# Revit family: AM 800 HTDE
name_source: partatom
category: Mechanical Equipment
units: mm (PartAtom-declared; Revit-internal decimal feet)

## family parameters
Always vertical = Yes
Cut with Voids When Loaded = No
OmniClass Number = 23.75.00.00
OmniClass Title = Climate Control (HVAC)
Part Type = Normal
Room Calculation Point = No
Round Connector Dimension = Use Diameter
Shared = No
Work Plane-Based = No

## types (1)
- AM 800 HTDE
    BMS IN = (PTS) 2x2x0,6
    BMS Out = (PTS) 2x2x0,6
    BMS Panel = (PTS) 2x2x0,6
    Condensate = 9 mm  [stored 0.0295276 ft]
    Electrical connection = 1 ~ 230 V / N / PE / 50 Hz
    Exhaust Air = 315 mm
    L-C Duct ESupply = 255 mm  [stored 0.836614 ft]
    Manufacturer = Airmaster A/S
    Max. flow rate 30 dB(A) with ePM10 50% filters = 650 m³
    Max. flow rate 30 dB(A) with ePM10 55% filters = 585 m³
    Max. flow rate 30 dB(A) with ePM10 80% filters = 520 m³
    Max. flow rate 35 dB(A) with ePM10 50% filters = 725 m³
    Max. flow rate 35 dB(A) with ePM10 55% filters = 653 m³
    Max. flow rate 35 dB(A) with ePM10 80% filters = 580 m³
    Model = AM 800 HTDE
    Network Conection = AWG 24 CAT 5e STP
    Nominal current, air handling unit = 1,1 A
    Nominal current, electrical comfort heating surface = 4,4 A
    Nominal current, electrical preheating surface = 6,5 A
    Phase 1 - Max Current = 12 A
    Phase 1 - Max Power Consumption = 4035 W
    R-C Duct Exhaust = 222 mm  [stored 0.728346 ft]
    Return Air Duct = 250 mm  [stored 0.82021 ft]
    Suply Air In = 315 mm
    T-C Duct Exhaust = 252 mm  [stored 0.826772 ft]
    T-C Duct Supply = 252 mm  [stored 0.826772 ft]
    Total Depth = 916 mm  [stored 3.00525 ft]
    Total Hight = 474 mm  [stored 1.55512 ft]
    Total Width = 1910 mm  [stored 6.2664 ft]
    URL = www.airmaster-as.com
    Water Heater Surface IN = 10 mm  [stored 0.0328084 ft]
    Water Heater Surface Return = 10 mm  [stored 0.0328084 ft]
    Weight (Standard Unit) = 108

note: [stored X ft] marks values corroborated as IEEE doubles in the binary element streams (Revit-internal decimal feet)

## geometry (parser evidence)
native form markers: Sweep x5
no freeform markers — native parametric forms only
